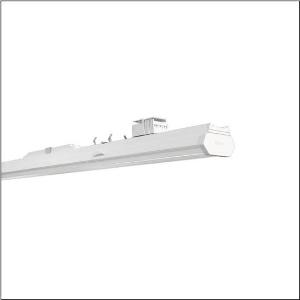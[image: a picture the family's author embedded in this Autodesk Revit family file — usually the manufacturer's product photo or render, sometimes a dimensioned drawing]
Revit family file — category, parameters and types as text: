
# Revit family: licross_r__11_protected_mo_51tp12dn495g_6914
name_source: partatom
category: Lighting Fixtures
units: mm (PartAtom-declared; Revit-internal decimal feet)

## family parameters
Cut with Voids When Loaded = No
Host = Face
Light Source = No
Part Type = Normal
Room Calculation Point = No
Round Connector Dimension = Use Diameter
Shared = No

## types (1)
- --- (1 x LED, 9980 lm, 57.1 W, 4000K)
    Apparent Load = 57 VA
    CIE Flux Codes = 73 92 98 99 100
    Color Rendering = 80
    Color Temperature = 4000K
    Default Elevation = 1800 mm
    Description = Licross® 11 Protected MO, luminaire insert, of sheet steel, galvanised, coil coated, white, length: 1.500mm, width: 90mm, height: 101mm, LED rated luminous flux: 9.980lm, light colour: 840, control gear: DALI 2, with plug, 5-pole, with phase selection, mains connection: 220..240V, AC, 50/60Hz, rated input power: 57W, halogen-free wiring, primary optical cover: cover, of PMMA, light emission: direct distribution, primary light characteristic: symmetric, protection rating (complete): IP64, insulation class (complete): insulation class I (protective earthing), certification: CE, ENEC, VDE, UKCA, protection symbol: D if used in an environment with conductive dust loads with corresponding accessories, impact resistance: IK06, permissible ambient temperature for indoor applications: -25..+35°C, corresponds to IFS (International Featured Standards) requirements for safety and quality in the food industry, reducing of maximum allowable ambient temperature of 5°C with ceiling mounting, LABS conformity tested according to VDMA 24364:2018-05, packaging unit: 1 piece
    Height = 92 mm
    Lamp = 1 x LED
    Lamp Light Flux = 9980 lm
    Lamp Power = 57.1 W
    Lamp count = 1
    Length = 1500 mm
    Luminous efficacy = 175 lm/W
    Manufacturer = Siteco
    ModVariant = No
    Model = 51TP12DN495G
    Mounting Place = Ceiling
    Mounting Type = Pendant
    Number of Poles = 1
    OnlyDefault = Yes
    Power Factor = 1
    Product Name = Licross® 11 Protected MO
    Product group = luminaire insert
    ProductGroupID = 901
    Protection Class = Protection class I
    Protection Degree = IP 64
    RLX_Detail_Level = 1
    RLX_Emergency_Light_Flux = 0 lm
    RLX_Emergency_Type = 0
    RLX_Emergency_Type_DB = No
    RlxData = <blob elided: 24373 chars, md5=123a2fec>
    Socket = socket
    Standby Power = 0 W
    System Light Flux = 9980 lm
    System Power = 57 W
    Type Comments = factory setting: luminous flux: 100 % | dim-lin: 254 | 378 mA
    Type Image = l_1256148.jpg
    URL = http://relux.com
    VarID = @adj_031225
    Voltage = 0 V
    Weight = 0.00 kg
    Width = 88 mm

## geometry (parser evidence)
native form markers: Blend x4, Sweep x9
no freeform markers — native parametric forms only
